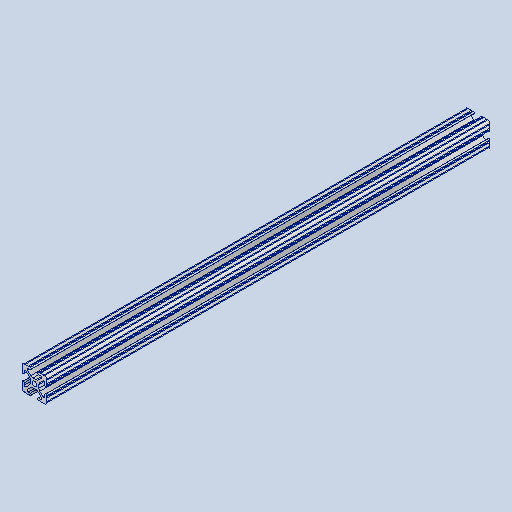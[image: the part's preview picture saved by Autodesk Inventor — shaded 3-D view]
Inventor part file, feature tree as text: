
AUTODESK INVENTOR PART (.ipt)
format: ipt  version: 2023 (Build 270158000, 158)  size: 499,200 bytes
history: native  units: in
note: dims shown in document units (in); Inventor stores cm internally (conversion verified against a paired STEP export)
features: extrude x1, sketch x1, projected_geometry x1, other x1
ambient origin geometry x8: Origin, YZ Plane, XZ Plane, XY Plane, X Axis, Y Axis, Z Axis, Center Point
bodies: Solid1 (feature_tree)
feature tree (4):
  extrude  "Extrusion1"  [1 undecoded]
  sketch  "Sketch1"  dims[d0=6.0in d1=0.0in]
  projected_geometry  "Projected Loop1"
  other  "Boss-Extrude1"
note: 1 required parameter value undecoded (feature->parameter linkage not recoverable at this tier; creation-order binding heuristic only, values carry confidence <= 0.55)
